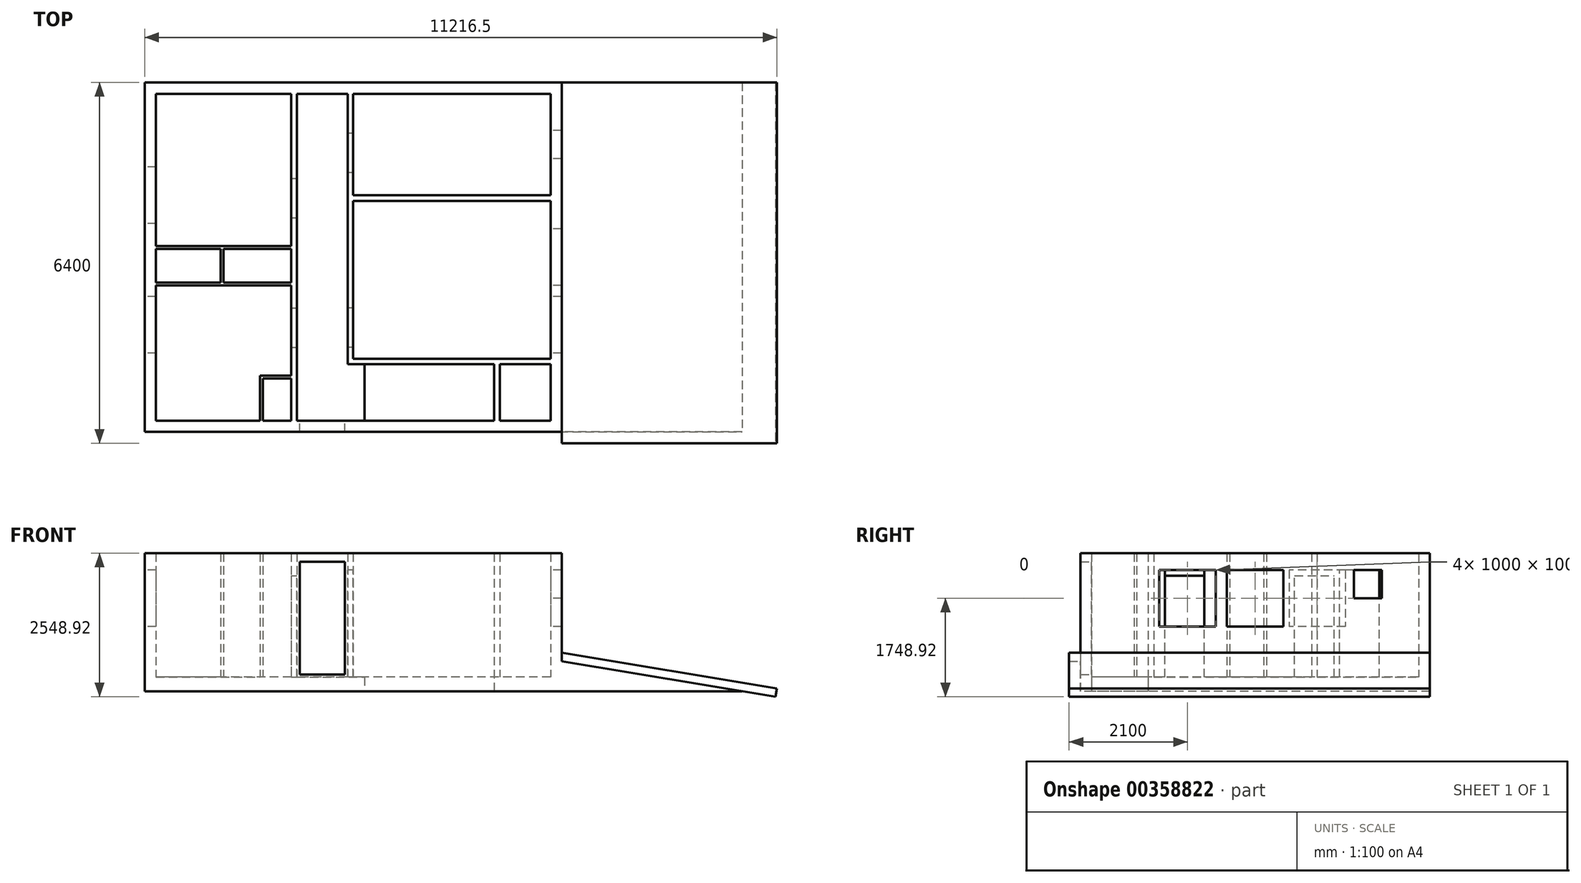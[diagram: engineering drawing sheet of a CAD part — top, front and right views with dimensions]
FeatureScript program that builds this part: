
annotation { "Feature Type Name" : "Feature", "Feature Type Description" : "" }
export const myFeature = defineFeature(function(context is Context, id is Id, definition is map)
    precondition{}
    {
        {
            var Q0;
            Q0=qCreatedBy(makeId("Top.planeOp"),FACE);
            var sketch = newSketch(context, id + "F0", { "sketchPlane" : qUnion([Q0])});
            skLineSegment(sketch, "E0.bottom", {"start": v(0, 0) * mm, "end": v(7400, 0) * mm});
            skLineSegment(sketch, "E0.top", {"start": v(0, -6200) * mm, "end": v(7400, -6200) * mm});
            skLineSegment(sketch, "E0.left", {"start": v(0, 0) * mm, "end": v(0, -6200) * mm});
            skLineSegment(sketch, "E0.right", {"start": v(7400, 0) * mm, "end": v(7400, -6200) * mm});
            skLineSegment(sketch, "E1.bottom", {"start": v(3900, -5000) * mm, "end": v(6200, -5000) * mm});
            skLineSegment(sketch, "E1.top", {"start": v(3900, -6000) * mm, "end": v(6200, -6000) * mm});
            skLineSegment(sketch, "E1.left", {"start": v(3900, -5000) * mm, "end": v(3900, -6000) * mm});
            skLineSegment(sketch, "E1.right", {"start": v(6200, -5000) * mm, "end": v(6200, -6000) * mm});
            skSolve(sketch);
        }
        {
            var Q0;
            Q0 = qSketchRegion(id + "F0", true);
            extrude(context, id + "F1", {"entities" : qUnion([Q0]), "depth" : 250 * mm});
        }
        {
            var Q0;
            Q0=makeQuery(id+"F1.opExtrude","CAP_FACE",FACE,{"disambiguationData":[OSD([sQuery(id+"F0.wireOp",EDGE,"E0.bottom"),sQuery(id+"F0.wireOp",EDGE,"E0.top"),sQuery(id+"F0.wireOp",EDGE,"E0.left"),sQuery(id+"F0.wireOp",EDGE,"E0.right"),sQuery(id+"F0.wireOp",EDGE,"E1.bottom"),sQuery(id+"F0.wireOp",EDGE,"E1.top"),sQuery(id+"F0.wireOp",EDGE,"E1.left"),sQuery(id+"F0.wireOp",EDGE,"E1.right")])],"isStart":false});
            var sketch = newSketch(context, id + "F2", { "sketchPlane" : qUnion([Q0])});
            skLineSegment(sketch, "E2.bottom", {"start": v(0, 0) * mm, "end": v(7400, 0) * mm});
            skLineSegment(sketch, "E2.top", {"start": v(0, -6200) * mm, "end": v(7400, -6200) * mm});
            skLineSegment(sketch, "E2.left", {"start": v(0, 0) * mm, "end": v(0, -6200) * mm});
            skLineSegment(sketch, "E2.right", {"start": v(7400, 0) * mm, "end": v(7400, -6200) * mm});
            skLineSegment(sketch, "E3.0", {"start": v(200, -200) * mm, "end": v(200, -2900) * mm});
            skLineSegment(sketch, "E3.1", {"start": v(7200, -200) * mm, "end": v(3700, -200) * mm});
            skLineSegment(sketch, "E3.3", {"start": v(2700, -6000) * mm, "end": v(6200, -6000) * mm});
            skLineSegment(sketch, "E4.top", {"start": v(7200, -2000) * mm, "end": v(3700, -2000) * mm});
            skLineSegment(sketch, "E5.bottom", {"start": v(7200, -2100) * mm, "end": v(3700, -2100) * mm});
            skLineSegment(sketch, "E5.top", {"start": v(7200, -4900) * mm, "end": v(3700, -4900) * mm});
            skLineSegment(sketch, "E6.top", {"start": v(7200, -5000) * mm, "end": v(6300, -5000) * mm});
            skLineSegment(sketch, "E6.left", {"start": v(7200, -6000) * mm, "end": v(7200, -5000) * mm});
            skLineSegment(sketch, "E6.right", {"start": v(6300, -6000) * mm, "end": v(6300, -5000) * mm});
            skLineSegment(sketch, "E7.top", {"start": v(200, -2900) * mm, "end": v(2600, -2900) * mm});
            skLineSegment(sketch, "E7.right", {"start": v(2600, -200) * mm, "end": v(2600, -2900) * mm});
            skLineSegment(sketch, "E8.top", {"start": v(200, -6000) * mm, "end": v(2050, -6000) * mm});
            skLineSegment(sketch, "E9.right", {"start": v(2700, -200) * mm, "end": v(2700, -6000) * mm});
            skLineSegment(sketch, "E10.trimOffspring", {"start": v(2600, -3600) * mm, "end": v(2600, -5200) * mm});
            skLineSegment(sketch, "E11.trimOffspring", {"start": v(3700, -2100) * mm, "end": v(3700, -4900) * mm});
            skLineSegment(sketch, "E12", {"start": v(6200, -6000) * mm, "end": v(6200, -5000) * mm});
            skLineSegment(sketch, "E13", {"start": v(6200, -5000) * mm, "end": v(3600, -5000) * mm});
            skLineSegment(sketch, "E14.trimOffspring", {"start": v(7200, -4900) * mm, "end": v(7200, -2100) * mm});
            skLineSegment(sketch, "E15.trimOffspring", {"start": v(7200, -2000) * mm, "end": v(7200, -200) * mm});
            skLineSegment(sketch, "E16.trimOffspring", {"start": v(2600, -200) * mm, "end": v(200, -200) * mm});
            skLineSegment(sketch, "E17.trimOffspring", {"start": v(3600, -200) * mm, "end": v(2700, -200) * mm});
            skLineSegment(sketch, "E18.trimOffspring", {"start": v(6300, -6000) * mm, "end": v(7200, -6000) * mm});
            skLineSegment(sketch, "E19", {"start": v(2600, -3600) * mm, "end": v(200, -3600) * mm});
            skLineSegment(sketch, "E20", {"start": v(200, -3600) * mm, "end": v(200, -6000) * mm});
            skLineSegment(sketch, "E21.bottom", {"start": v(2600, -2950) * mm, "end": v(1400, -2950) * mm});
            skLineSegment(sketch, "E21.top", {"start": v(2600, -3550) * mm, "end": v(1400, -3550) * mm});
            skLineSegment(sketch, "E21.left", {"start": v(2600, -2950) * mm, "end": v(2600, -3550) * mm});
            skLineSegment(sketch, "E21.right", {"start": v(1400, -2950) * mm, "end": v(1400, -3550) * mm});
            skLineSegment(sketch, "E22.bottom", {"start": v(1350, -2950) * mm, "end": v(200, -2950) * mm});
            skLineSegment(sketch, "E22.top", {"start": v(1350, -3550) * mm, "end": v(200, -3550) * mm});
            skLineSegment(sketch, "E22.left", {"start": v(1350, -2950) * mm, "end": v(1350, -3550) * mm});
            skLineSegment(sketch, "E22.right", {"start": v(200, -2950) * mm, "end": v(200, -3550) * mm});
            skLineSegment(sketch, "E23", {"start": v(2600, -5250) * mm, "end": v(2100, -5250) * mm});
            skLineSegment(sketch, "E24", {"start": v(2100, -5250) * mm, "end": v(2100, -6000) * mm});
            skLineSegment(sketch, "E25.0", {"start": v(2050, -5200) * mm, "end": v(2050, -6000) * mm});
            skLineSegment(sketch, "E25.1", {"start": v(2600, -5200) * mm, "end": v(2050, -5200) * mm});
            skLineSegment(sketch, "E26.trimOffspring", {"start": v(2100, -6000) * mm, "end": v(2600, -6000) * mm});
            skLineSegment(sketch, "E27.trimOffspring", {"start": v(2600, -5250) * mm, "end": v(2600, -6000) * mm});
            skLineSegment(sketch, "E28", {"start": v(3600, -200) * mm, "end": v(3600, -5000) * mm});
            skLineSegment(sketch, "E29", {"start": v(3700, -200) * mm, "end": v(3700, -2000) * mm});
            skSolve(sketch);
        }
        {
            var Q0;
            Q0 = qSketchRegion(id + "F2", true);
            extrude(context, id + "F3", {"entities" : qUnion([Q0]), "operationType" : NewBodyOperationType.ADD, "depth" : 2200 * mm});
        }
        {
            var Q0;
            Q0=makeQuery(id+"F3.boolean.opBoolean","MERGE",FACE,{"derivedFrom":[makeQuery(id+"F1.opExtrude","SWEPT_FACE",FACE,{"disambiguationData":[OSD([sQuery(id+"F0.wireOp",EDGE,"E0.top")])]}),makeQuery(id+"F3.opExtrude","SWEPT_FACE",FACE,{"disambiguationData":[OSD([sQuery(id+"F2.wireOp",EDGE,"E2.top")])]})]});
            var sketch = newSketch(context, id + "F4", { "sketchPlane" : qUnion([Q0])});
            skLineSegment(sketch, "E30", {"start": v(10600, 0) * mm, "end": v(11191.8, -98.92) * mm});
            skLineSegment(sketch, "E31", {"start": v(11191.8, -98.92) * mm, "end": v(11216.52, 49.03) * mm});
            skLineSegment(sketch, "E32", {"start": v(11216.52, 49.03) * mm, "end": v(7400, 686.95) * mm});
            skLineSegment(sketch, "E33", {"start": v(7400, 0) * mm, "end": v(7400, 686.95) * mm});
            skLineSegment(sketch, "E34", {"start": v(7400, 0) * mm, "end": v(10600, 0) * mm});
            skSolve(sketch);
        }
        {
            var Q0;
            Q0 = qSketchRegion(id + "F4", true);
            var Q1;
            Q1=makeQuery(id+"F3.boolean.opBoolean","MERGE",FACE,{"derivedFrom":[makeQuery(id+"F1.opExtrude","SWEPT_FACE",FACE,{"disambiguationData":[OSD([sQuery(id+"F0.wireOp",EDGE,"E0.bottom")])]}),makeQuery(id+"F3.opExtrude","SWEPT_FACE",FACE,{"disambiguationData":[OSD([sQuery(id+"F2.wireOp",EDGE,"E2.bottom")])]})]});
            extrude(context, id + "F5", {"entities" : qUnion([Q0]), "operationType" : NewBodyOperationType.ADD, "endBound" : BoundingType.UP_TO_SURFACE, "oppositeDirection" : true, "endBoundEntityFace" : qUnion([Q1]), "depth" : 25 * mm});
        }
        {
            var Q0;
            Q0=makeQuery(id+"F3.opExtrude","SWEPT_FACE",FACE,{"disambiguationData":[OSD([sQuery(id+"F2.wireOp",EDGE,"E9.right")])]});
            var sketch = newSketch(context, id + "F6", { "sketchPlane" : qUnion([Q0])});
            skLineSegment(sketch, "E35.bottom", {"start": v(-4700, 250) * mm, "end": v(-4000, 250) * mm});
            skLineSegment(sketch, "E35.top", {"start": v(-4700, 2050) * mm, "end": v(-4000, 2050) * mm});
            skLineSegment(sketch, "E35.left", {"start": v(-4700, 250) * mm, "end": v(-4700, 2050) * mm});
            skLineSegment(sketch, "E35.right", {"start": v(-4000, 250) * mm, "end": v(-4000, 2050) * mm});
            skLineSegment(sketch, "E36.bottom", {"start": v(-2400, 250) * mm, "end": v(-1700, 250) * mm});
            skLineSegment(sketch, "E36.top", {"start": v(-2400, 2050) * mm, "end": v(-1700, 2050) * mm});
            skLineSegment(sketch, "E36.left", {"start": v(-2400, 250) * mm, "end": v(-2400, 2050) * mm});
            skLineSegment(sketch, "E36.right", {"start": v(-1700, 250) * mm, "end": v(-1700, 2050) * mm});
            skSolve(sketch);
        }
        {
            var Q0;
            Q0 = qSketchRegion(id + "F6", true);
            extrude(context, id + "F7", {"entities" : qUnion([Q0]), "operationType" : NewBodyOperationType.REMOVE, "endBound" : BoundingType.UP_TO_NEXT, "oppositeDirection" : true, "depth" : 25 * mm});
        }
        {
            var Q0;
            Q0=makeQuery(id+"F3.opExtrude","SWEPT_FACE",FACE,{"disambiguationData":[OSD([sQuery(id+"F2.wireOp",EDGE,"E28")])]});
            var sketch = newSketch(context, id + "F8", { "sketchPlane" : qUnion([Q0])});
            skLineSegment(sketch, "E37.bottom", {"start": v(900, 250) * mm, "end": v(1600, 250) * mm});
            skLineSegment(sketch, "E37.top", {"start": v(900, 2150) * mm, "end": v(1600, 2150) * mm});
            skLineSegment(sketch, "E37.left", {"start": v(900, 250) * mm, "end": v(900, 2150) * mm});
            skLineSegment(sketch, "E37.right", {"start": v(1600, 250) * mm, "end": v(1600, 2150) * mm});
            skLineSegment(sketch, "E38.bottom", {"start": v(4000, 250) * mm, "end": v(4700, 250) * mm});
            skLineSegment(sketch, "E38.top", {"start": v(4000, 2150) * mm, "end": v(4700, 2150) * mm});
            skLineSegment(sketch, "E38.left", {"start": v(4000, 250) * mm, "end": v(4000, 2150) * mm});
            skLineSegment(sketch, "E38.right", {"start": v(4700, 250) * mm, "end": v(4700, 2150) * mm});
            skSolve(sketch);
        }
        {
            var Q0;
            Q0 = qSketchRegion(id + "F8", true);
            extrude(context, id + "F9", {"entities" : qUnion([Q0]), "operationType" : NewBodyOperationType.REMOVE, "endBound" : BoundingType.UP_TO_NEXT, "oppositeDirection" : true, "depth" : 25 * mm});
        }
        {
            var Q0;
            Q0=makeQuery(id+"F3.opExtrude","SWEPT_FACE",FACE,{"disambiguationData":[OSD([sQuery(id+"F2.wireOp",EDGE,"E14.trimOffspring")])]});
            var sketch = newSketch(context, id + "F10", { "sketchPlane" : qUnion([Q0])});
            skLineSegment(sketch, "E39.bottom", {"start": v(2600, 2150) * mm, "end": v(3600, 2150) * mm});
            skLineSegment(sketch, "E39.top", {"start": v(2600, 1150) * mm, "end": v(3600, 1150) * mm});
            skLineSegment(sketch, "E39.left", {"start": v(2600, 2150) * mm, "end": v(2600, 1150) * mm});
            skLineSegment(sketch, "E39.right", {"start": v(3600, 2150) * mm, "end": v(3600, 1150) * mm});
            skLineSegment(sketch, "E40.bottom", {"start": v(3800, 2150) * mm, "end": v(4800, 2150) * mm});
            skLineSegment(sketch, "E40.top", {"start": v(3800, 1150) * mm, "end": v(4800, 1150) * mm});
            skLineSegment(sketch, "E40.left", {"start": v(3800, 2150) * mm, "end": v(3800, 1150) * mm});
            skLineSegment(sketch, "E40.right", {"start": v(4800, 2150) * mm, "end": v(4800, 1150) * mm});
            skLineSegment(sketch, "E41.bottom", {"start": v(1350, 2150) * mm, "end": v(850, 2150) * mm});
            skLineSegment(sketch, "E41.top", {"start": v(1350, 1650) * mm, "end": v(850, 1650) * mm});
            skLineSegment(sketch, "E41.left", {"start": v(1350, 2150) * mm, "end": v(1350, 1650) * mm});
            skLineSegment(sketch, "E41.right", {"start": v(850, 2150) * mm, "end": v(850, 1650) * mm});
            skSolve(sketch);
        }
        {
            var Q0;
            Q0 = qSketchRegion(id + "F10", true);
            extrude(context, id + "F11", {"entities" : qUnion([Q0]), "operationType" : NewBodyOperationType.REMOVE, "endBound" : BoundingType.UP_TO_NEXT, "oppositeDirection" : true, "depth" : 25 * mm});
        }
        {
            var Q0;
            Q0=makeQuery(id+"F3.boolean.opBoolean","MERGE",FACE,{"derivedFrom":[makeQuery(id+"F1.opExtrude","SWEPT_FACE",FACE,{"disambiguationData":[OSD([sQuery(id+"F0.wireOp",EDGE,"E0.left")])]}),makeQuery(id+"F3.opExtrude","SWEPT_FACE",FACE,{"disambiguationData":[OSD([sQuery(id+"F2.wireOp",EDGE,"E2.left")])]})]});
            var sketch = newSketch(context, id + "F12", { "sketchPlane" : qUnion([Q0])});
            skLineSegment(sketch, "E42.bottom", {"start": v(1500, 2150) * mm, "end": v(2500, 2150) * mm});
            skLineSegment(sketch, "E42.top", {"start": v(1500, 1150) * mm, "end": v(2500, 1150) * mm});
            skLineSegment(sketch, "E42.left", {"start": v(1500, 2150) * mm, "end": v(1500, 1150) * mm});
            skLineSegment(sketch, "E42.right", {"start": v(2500, 2150) * mm, "end": v(2500, 1150) * mm});
            skLineSegment(sketch, "E43.bottom", {"start": v(3800, 2150) * mm, "end": v(4800, 2150) * mm});
            skLineSegment(sketch, "E43.top", {"start": v(3800, 1150) * mm, "end": v(4800, 1150) * mm});
            skLineSegment(sketch, "E43.left", {"start": v(3800, 2150) * mm, "end": v(3800, 1150) * mm});
            skLineSegment(sketch, "E43.right", {"start": v(4800, 2150) * mm, "end": v(4800, 1150) * mm});
            skSolve(sketch);
        }
        {
            var Q0;
            Q0 = qSketchRegion(id + "F12", true);
            extrude(context, id + "F13", {"entities" : qUnion([Q0]), "operationType" : NewBodyOperationType.REMOVE, "endBound" : BoundingType.UP_TO_NEXT, "oppositeDirection" : true, "depth" : 25 * mm});
        }
        {
            var Q0;
            Q0=makeQuery(id+"F3.boolean.opBoolean","MERGE",FACE,{"derivedFrom":[makeQuery(id+"F1.opExtrude","SWEPT_FACE",FACE,{"disambiguationData":[OSD([sQuery(id+"F0.wireOp",EDGE,"E1.top")])]}),makeQuery(id+"F3.opExtrude","SWEPT_FACE",FACE,{"disambiguationData":[OSD([sQuery(id+"F2.wireOp",EDGE,"E3.3")])]})]});
            var sketch = newSketch(context, id + "F14", { "sketchPlane" : qUnion([Q0])});
            skLineSegment(sketch, "E44.bottom", {"start": v(-2750, 300) * mm, "end": v(-3550, 300) * mm});
            skLineSegment(sketch, "E44.top", {"start": v(-2750, 2300) * mm, "end": v(-3550, 2300) * mm});
            skLineSegment(sketch, "E44.left", {"start": v(-2750, 300) * mm, "end": v(-2750, 2300) * mm});
            skLineSegment(sketch, "E44.right", {"start": v(-3550, 300) * mm, "end": v(-3550, 2300) * mm});
            skSolve(sketch);
        }
        {
            var Q0;
            Q0 = qSketchRegion(id + "F14", true);
            extrude(context, id + "F15", {"entities" : qUnion([Q0]), "operationType" : NewBodyOperationType.REMOVE, "endBound" : BoundingType.UP_TO_NEXT, "oppositeDirection" : true, "depth" : 25 * mm});
        }
        {
            var Q0;
            Q0=makeQuery(id+"F5.boolean.opBoolean","MERGE",FACE,{"derivedFrom":[makeQuery(id+"F3.boolean.opBoolean","MERGE",FACE,{"derivedFrom":[makeQuery(id+"F1.opExtrude","SWEPT_FACE",FACE,{"disambiguationData":[OSD([sQuery(id+"F0.wireOp",EDGE,"E0.top")])]}),makeQuery(id+"F3.opExtrude","SWEPT_FACE",FACE,{"disambiguationData":[OSD([sQuery(id+"F2.wireOp",EDGE,"E2.top")])]})]}),makeQuery(id+"F5.opExtrude","CAP_FACE",FACE,{"disambiguationData":[OSD([sQuery(id+"F4.wireOp",EDGE,"E30"),sQuery(id+"F4.wireOp",EDGE,"E31"),sQuery(id+"F4.wireOp",EDGE,"E32"),sQuery(id+"F4.wireOp",EDGE,"E33"),sQuery(id+"F4.wireOp",EDGE,"E34")])],"isStart":true})]});
            var sketch = newSketch(context, id + "F16", { "sketchPlane" : qUnion([Q0])});
            skLineSegment(sketch, "E45.0", {"start": v(11191.8, -98.92) * mm, "end": v(11216.52, 49.03) * mm});
            skLineSegment(sketch, "E46.0", {"start": v(11216.52, 49.03) * mm, "end": v(7400, 686.95) * mm});
            skLineSegment(sketch, "E47.0", {"start": v(11191.8, -98.92) * mm, "end": v(7400, 534.87) * mm});
            skLineSegment(sketch, "E48", {"start": v(7400, 686.95) * mm, "end": v(7400, 534.87) * mm});
            skSolve(sketch);
        }
        {
            var Q0;
            Q0 = qSketchRegion(id + "F16", true);
            extrude(context, id + "F17", {"entities" : qUnion([Q0]), "operationType" : NewBodyOperationType.ADD, "depth" : 200 * mm});
        }
    });
